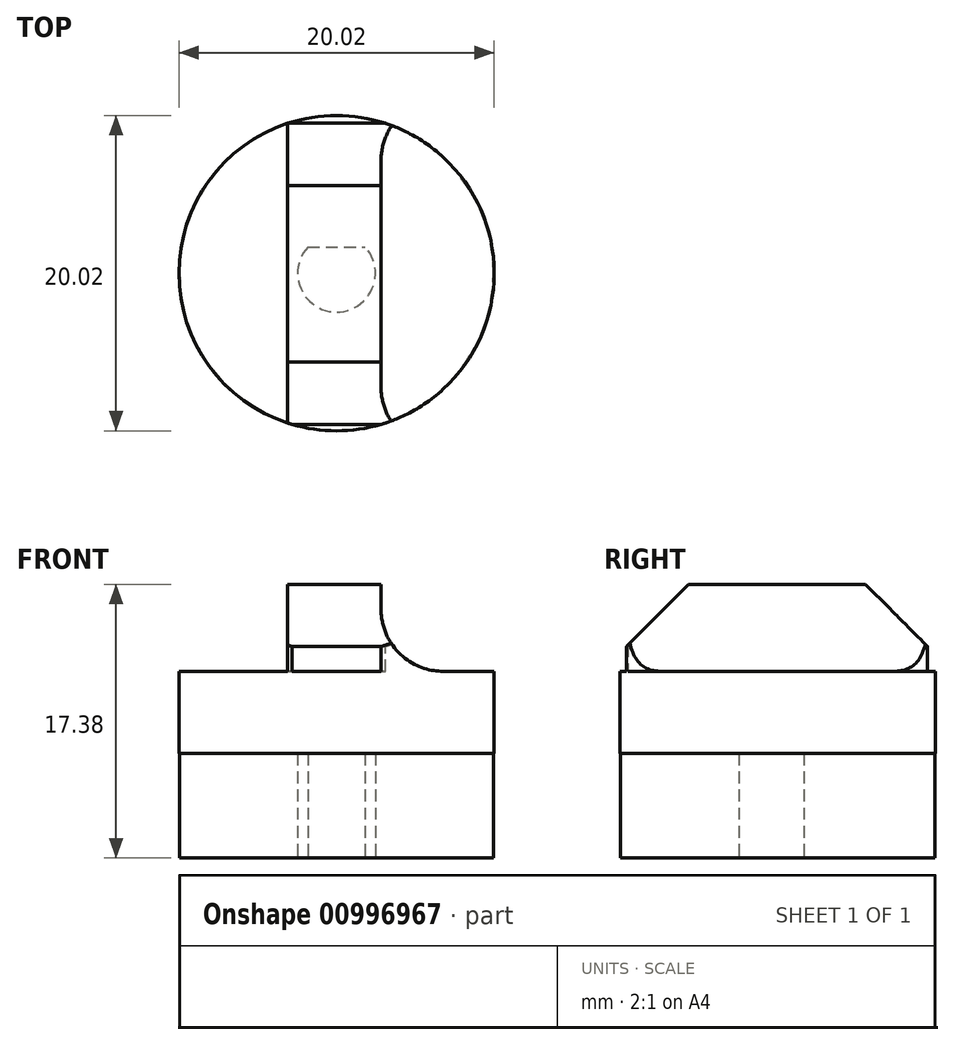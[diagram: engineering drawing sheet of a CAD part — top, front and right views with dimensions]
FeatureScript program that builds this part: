
annotation { "Feature Type Name" : "Feature", "Feature Type Description" : "" }
export const myFeature = defineFeature(function(context is Context, id is Id, definition is map)
    precondition{}
    {
        {
            var Q0;
            Q0=qCreatedBy(makeId("Top.planeOp"),FACE);
            var sketch = newSketch(context, id + "F0", { "sketchPlane" : qUnion([Q0])});
            skCircle(sketch, "E0", {"center": v(0, 0) * mm, "radius": 12.62 * mm});
            skCircle(sketch, "E1.0", {"center": v(0, 0) * mm, "radius": 10.38 * mm});
            skCircle(sketch, "E2", {"center": v(0, 0) * mm, "radius": 5 * mm});
            skCircle(sketch, "E3", {"center": v(0, 0) * mm, "radius": 3.12 * mm});
            skLineSegment(sketch, "E4", {"start": v(-2.3, 2.11) * mm, "end": v(2.3, 2.11) * mm});
            skSolve(sketch);
        }
        {
            var Q0;
            Q0=makeQuery(id+"F0.imprint","IMPRINT",FACE,{"disambiguationData":[TD([[makeQuery(id+"F0.imprint","IMPRINT",EDGE,{"derivedFrom":sQuery(id+"F0.wireOp",EDGE,"E1.0")}),1.0]])]});
            var Q1;
            Q1=makeQuery(id+"F0.imprint","IMPRINT",FACE,{"disambiguationData":[TD([[makeQuery(id+"F0.imprint","IMPRINT",EDGE,{"derivedFrom":sQuery(id+"F0.wireOp",EDGE,"E0")}),1.0]])]});
            extrude(context, id + "F1", {"entities" : qUnion([Q0, Q1]), "depth" : 15 * mm});
        }
        {
            var Q0;
            Q0=makeQuery(id+"F0.imprint","IMPRINT",FACE,{"disambiguationData":[TD([[makeQuery(id+"F0.imprint","IMPRINT",EDGE,{"derivedFrom":sQuery(id+"F0.wireOp",EDGE,"E2")}),1.0]])]});
            var Q1;
            {var subQ0=sQuery(id+"F0.wireOp",EDGE,"kcsZYRUV-fOb9-CoZI-3tOm-9hxGfB4E4ohr");Q1=makeQuery(id+"F0.imprint","IMPRINT",FACE,{"disambiguationData":[TD([[makeQuery(id+"F0.imprint","IMPRINT",EDGE,{"derivedFrom":subQ0}),-1.0]])]});}
            var Q2;
            {var subQ0=sQuery(id+"F0.wireOp",EDGE,"E4");Q2=makeQuery(id+"F0.imprint","IMPRINT",FACE,{"disambiguationData":[TD([[makeQuery(id+"F0.imprint","IMPRINT",EDGE,{"derivedFrom":subQ0}),1.0]])]});}
            extrude(context, id + "F2", {"entities" : qUnion([Q0, Q1, Q2]), "operationType" : NewBodyOperationType.ADD, "depth" : 15 * mm});
        }
        {
            var Q0;
            {var subQ0=sQuery(id+"F0.wireOp",EDGE,"E2");Q0=makeQuery(id+"F2.boolean.opBoolean","MERGE",FACE,{"derivedFrom":[makeQuery(id+"F1.opExtrude","CAP_FACE",FACE,{"disambiguationData":[OSD([sQuery(id+"F0.wireOp",EDGE,"E0"),subQ0])],"isStart":false}),makeQuery(id+"F2.opExtrude","CAP_FACE",FACE,{"disambiguationData":[OSD([subQ0,sQuery(id+"F0.wireOp",EDGE,"E3"),sQuery(id+"F0.wireOp",EDGE,"kcsZYRUV-fOb9-CoZI-3tOm-9hxGfB4E4ohr")])],"isStart":false})]});}
            var sketch = newSketch(context, id + "F3", { "sketchPlane" : qUnion([Q0])});
            skCircle(sketch, "E5", {"center": v(0, 0) * mm, "radius": 12.67 * mm});
            skSolve(sketch);
        }
        {
            var Q0;
            Q0=qSketchRegion(id+"F3",true);
            extrude(context, id + "F4", {"entities" : qUnion([Q0]), "operationType" : NewBodyOperationType.ADD, "oppositeDirection" : true, "depth" : 6.6 * mm});
        }
        {
            var Q0;
            {var subQ0=sQuery(id+"F0.wireOp",EDGE,"E2");Q0=makeQuery(id+"F4.boolean.opBoolean","MERGE",FACE,{"derivedFrom":[makeQuery(id+"F2.boolean.opBoolean","MERGE",FACE,{"derivedFrom":[makeQuery(id+"F1.opExtrude","CAP_FACE",FACE,{"disambiguationData":[OSD([sQuery(id+"F0.wireOp",EDGE,"E0"),subQ0])],"isStart":false}),makeQuery(id+"F2.opExtrude","CAP_FACE",FACE,{"disambiguationData":[OSD([subQ0,sQuery(id+"F0.wireOp",EDGE,"E3"),sQuery(id+"F0.wireOp",EDGE,"kcsZYRUV-fOb9-CoZI-3tOm-9hxGfB4E4ohr")])],"isStart":false})]}),makeQuery(id+"F4.opExtrude","CAP_FACE",FACE,{"disambiguationData":[OSD([sQuery(id+"F3.wireOp",EDGE,"E5")])],"isStart":true})]});}
            var sketch = newSketch(context, id + "F5", { "sketchPlane" : qUnion([Q0])});
            skLineSegment(sketch, "E6.bottom", {"start": v(-3.92, 12.05) * mm, "end": v(3.58, 12.05) * mm});
            skLineSegment(sketch, "E6.top", {"start": v(-3.92, -12.16) * mm, "end": v(3.58, -12.16) * mm});
            skLineSegment(sketch, "E6.left", {"start": v(-3.92, 12.05) * mm, "end": v(-3.92, -12.16) * mm});
            skLineSegment(sketch, "E6.right", {"start": v(3.58, 12.05) * mm, "end": v(3.58, -12.16) * mm});
            skSolve(sketch);
        }
        {
            var Q0;
            {var subQ1=sQuery(id+"F5.wireOp",EDGE,"E6.bottom");Q0=makeQuery(id+"F5.imprint","IMPRINT",FACE,{"disambiguationData":[TD([[makeQuery(id+"F5.imprint","IMPRINT",EDGE,{"derivedFrom":subQ1}),-1.0]])]});}
            extrude(context, id + "F6", {"entities" : qUnion([Q0]), "operationType" : NewBodyOperationType.ADD, "depth" : 7 * mm});
        }
        {
            var Q0;
            Q0=makeQuery(id+"F6.opExtrude","CAP_EDGE",EDGE,{"disambiguationData":[OSD([sQuery(id+"F5.wireOp",EDGE,"E6.left")])],"isStart":true});
            var Q1;
            Q1=makeQuery(id+"F6.opExtrude","CAP_EDGE",EDGE,{"disambiguationData":[OSD([sQuery(id+"F5.wireOp",EDGE,"E6.right")])],"isStart":true});
            fillet(context, id + "F7", {"entities" : qUnion([Q0, Q1]), "radius" : 5 * mm, "tangentPropagation" : true, "allowEdgeOverflow" : false});
        }
        {
            var Q0;
            Q0=makeQuery(id+"F6.opExtrude","CAP_EDGE",EDGE,{"disambiguationData":[OSD([sQuery(id+"F5.wireOp",EDGE,"E6.top")])],"isStart":false});
            chamfer(context, id + "F8", {"entities" : qUnion([Q0]), "width" : 5 * mm, "tangentPropagation" : true});
        }
        {
            var Q0;
            Q0=makeQuery(id+"F6.opExtrude","CAP_EDGE",EDGE,{"disambiguationData":[OSD([sQuery(id+"F5.wireOp",EDGE,"E6.bottom")])],"isStart":false});
            chamfer(context, id + "F9", {"entities" : qUnion([Q0]), "width" : 5 * mm, "tangentPropagation" : true});
        }
        {
            var Q0;
            Q0=makeQuery(id+"F1.opExtrude","SWEPT_BODY",BODY,{"disambiguationData":[OSD([sQuery(id+"F0.wireOp",EDGE,"E0"),sQuery(id+"F0.wireOp",EDGE,"E2")])]});
            var Q1;
            Q1=qCreatedBy(makeId("Origin.pointOp"),VERTEX);
            transform(context, id + "F10", {"entities" : qUnion([Q0]), "transformType" : TransformType.SCALE_UNIFORMLY, "scale" : 0.79, "scalePoint" : qUnion([Q1]), "makeCopy" : false});
        }
    });
